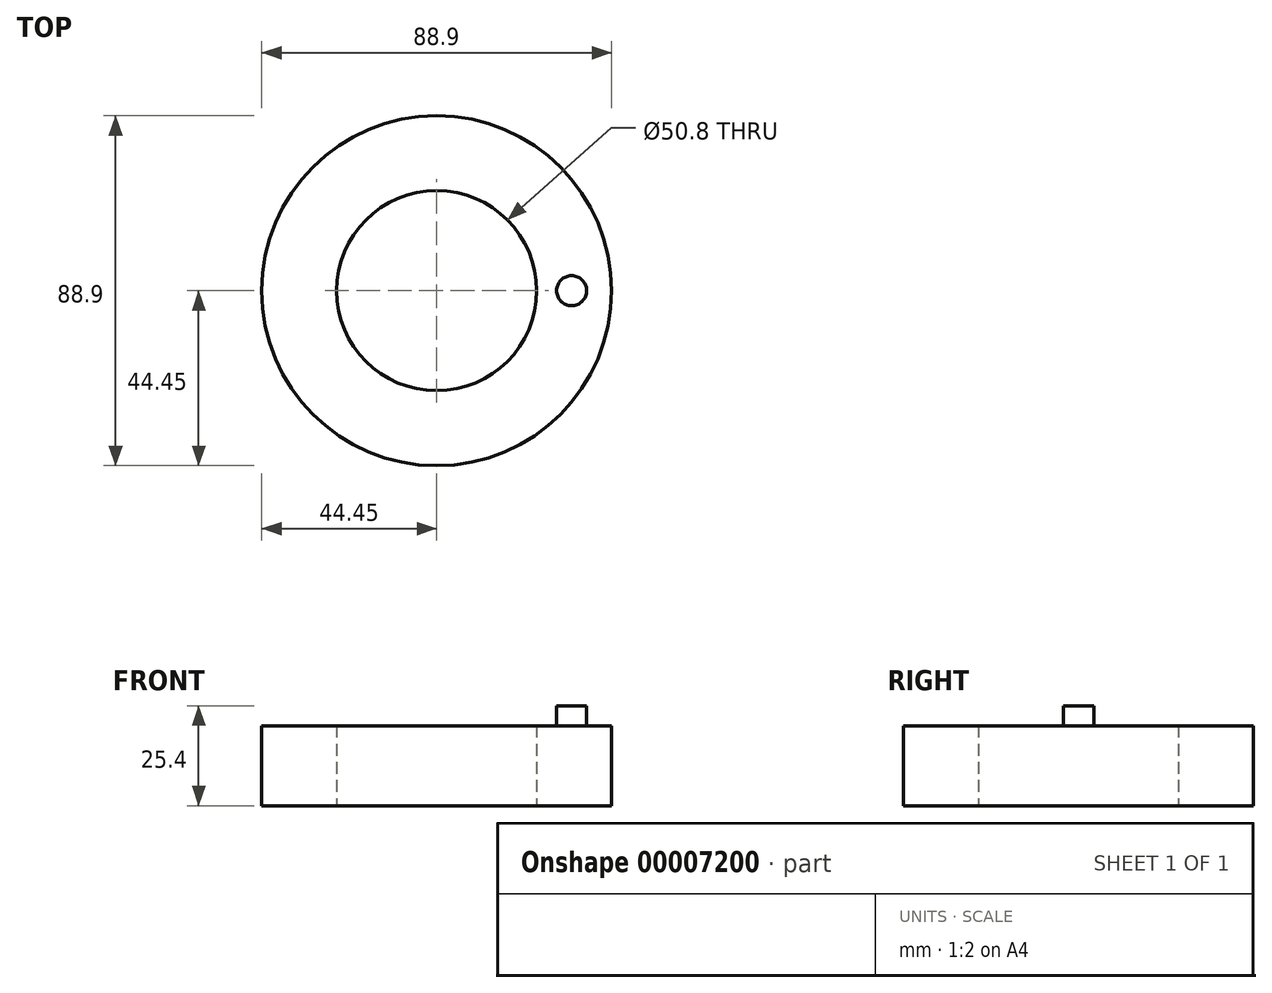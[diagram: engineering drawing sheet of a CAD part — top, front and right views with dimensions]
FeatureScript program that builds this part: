
annotation { "Feature Type Name" : "Feature", "Feature Type Description" : "" }
export const myFeature = defineFeature(function(context is Context, id is Id, definition is map)
    precondition{}
    {
        {
            var Q0;
            Q0=qCreatedBy(makeId("Top.planeOp"),FACE);
            var sketch = newSketch(context, id + "F0", { "sketchPlane" : qUnion([Q0])});
            skCircle(sketch, "E0", {"center": v(0, 0) * mm, "radius": 44.45 * mm});
            skCircle(sketch, "E1", {"center": v(0, 0) * mm, "radius": 25.4 * mm});
            skSolve(sketch);
        }
        {
            var Q0;
            Q0=sQuery(id+"F0.wireOp",EDGE,"E1");
            extrude(context, id + "F1", {"bodyType" : ToolBodyType.SURFACE, "surfaceEntities" : qUnion([Q0]), "depth" : 4 * mm});
        }
        {
            var Q0;
            Q0=makeQuery(id+"F0.imprint","IMPRINT",FACE,{"disambiguationData":[TD([[makeQuery(id+"F0.imprint","IMPRINT",EDGE,{"derivedFrom":sQuery(id+"F0.wireOp",EDGE,"E0")}),1.0]])]});
            extrude(context, id + "F2", {"entities" : qUnion([Q0]), "depth" : 25.4 * mm});
        }
        {
            var Q0;
            Q0=makeQuery(id+"F2.opExtrude","CAP_FACE",FACE,{"disambiguationData":[OSD([sQuery(id+"F0.wireOp",EDGE,"E0"),sQuery(id+"F0.wireOp",EDGE,"E1")])],"isStart":false});
            var sketch = newSketch(context, id + "F3", { "sketchPlane" : qUnion([Q0])});
            skCircle(sketch, "E2", {"center": v(-34.3, 0) * mm, "radius": 3.81 * mm});
            skCircle(sketch, "E3.MirrorC", {"center": v(34.3, 0) * mm, "radius": 3.81 * mm});
            skSolve(sketch);
        }
        {
            var Q0;
            Q0=makeQuery(id+"F3.imprint","IMPRINT",FACE,{"disambiguationData":[TD([[makeQuery(id+"F3.imprint","IMPRINT",EDGE,{"derivedFrom":sQuery(id+"F3.wireOp",EDGE,"E2")}),1.0]])]});
            extrude(context, id + "F4", {"entities" : qUnion([Q0]), "operationType" : NewBodyOperationType.REMOVE, "oppositeDirection" : true, "depth" : 5.08 * mm});
        }
        {
            var Q0;
            Q0=makeQuery(id+"F3.imprint","IMPRINT",FACE,{"disambiguationData":[TD([[makeQuery(id+"F3.imprint","IMPRINT",EDGE,{"derivedFrom":sQuery(id+"F3.wireOp",EDGE,"E3.MirrorC")}),-1.0]])]});
            extrude(context, id + "F5", {"entities" : qUnion([Q0]), "operationType" : NewBodyOperationType.REMOVE, "oppositeDirection" : true, "depth" : 5.08 * mm});
        }
    });
